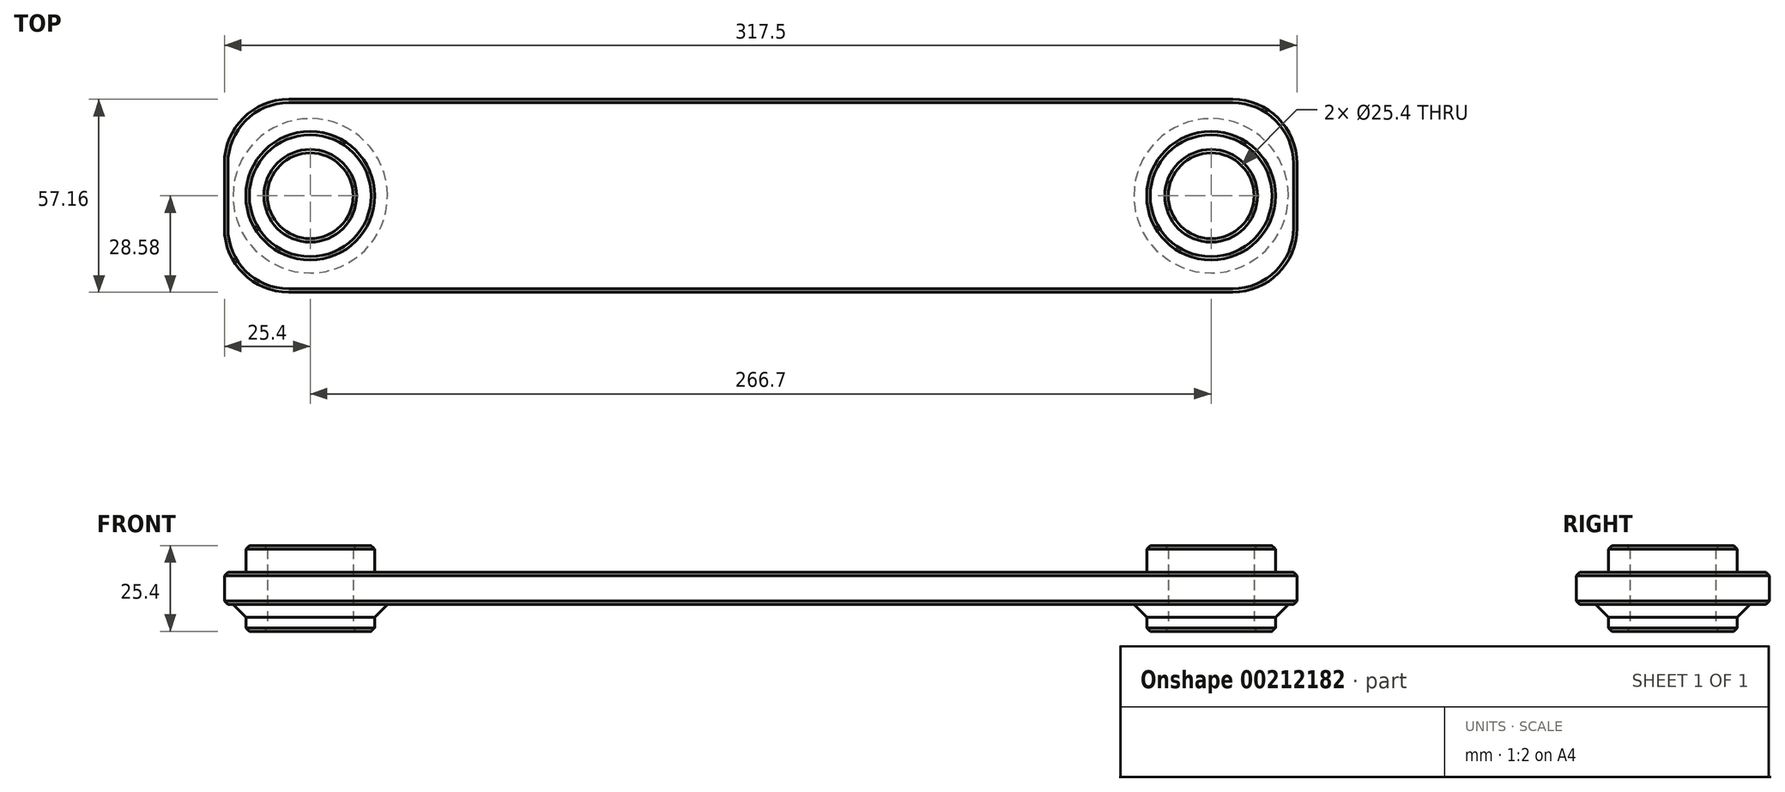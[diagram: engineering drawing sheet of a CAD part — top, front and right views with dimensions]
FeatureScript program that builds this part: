
annotation { "Feature Type Name" : "Feature", "Feature Type Description" : "" }
export const myFeature = defineFeature(function(context is Context, id is Id, definition is map)
    precondition{}
    {
        {
            var Q0;
            Q0=qCreatedBy(makeId("Top.planeOp"),FACE);
            var sketch = newSketch(context, id + "F0", { "sketchPlane" : qUnion([Q0])});
            skLineSegment(sketch, "E0.bottom", {"start": v(139.7, -28.57) * mm, "end": v(-139.7, -28.58) * mm});
            skLineSegment(sketch, "E0.top", {"start": v(139.7, 28.58) * mm, "end": v(-139.7, 28.57) * mm});
            skLineSegment(sketch, "E0.left", {"start": v(158.75, -9.52) * mm, "end": v(158.75, 9.53) * mm});
            skLineSegment(sketch, "E0.right", {"start": v(-158.75, -9.53) * mm, "end": v(-158.75, 9.52) * mm});
            skPoint(sketch, "E0.middle", {"position": v(0, 0) * mm});
            skCircle(sketch, "E1", {"center": v(133.35, 0) * mm, "radius": 12.7 * mm});
            skCircle(sketch, "E2", {"center": v(-133.35, 0) * mm, "radius": 12.7 * mm});
            skLineSegment(sketch, "E3", {"start": v(-133.35, 0) * mm, "end": v(0, 0) * mm, "construction": true});
            skLineSegment(sketch, "E4", {"start": v(0, 0) * mm, "end": v(133.35, 0) * mm, "construction": true});
            skCircle(sketch, "E5", {"center": v(133.35, 0) * mm, "radius": 19.05 * mm});
            skCircle(sketch, "E6", {"center": v(-133.35, 0) * mm, "radius": 19.05 * mm});
            skPoint(sketch, "E7.visualSharp", {"position": v(158.75, -28.57) * mm});
            skArc(sketch, "E7.filletArc", {"start": v(139.7, -28.57) * mm, "mid": v(153.17, -23) * mm, "end": v(158.75, -9.52) * mm});
            skPoint(sketch, "E8.visualSharp", {"position": v(158.75, 28.58) * mm});
            skArc(sketch, "E8.filletArc", {"start": v(158.75, 9.53) * mm, "mid": v(153.17, 23) * mm, "end": v(139.7, 28.58) * mm});
            skPoint(sketch, "E9.visualSharp", {"position": v(-158.75, -28.58) * mm});
            skArc(sketch, "E9.filletArc", {"start": v(-158.75, -9.53) * mm, "mid": v(-153.17, -23) * mm, "end": v(-139.7, -28.58) * mm});
            skPoint(sketch, "E10.visualSharp", {"position": v(-158.75, 28.57) * mm});
            skArc(sketch, "E10.filletArc", {"start": v(-139.7, 28.57) * mm, "mid": v(-153.17, 23) * mm, "end": v(-158.75, 9.52) * mm});
            skSolve(sketch);
        }
        {
            var Q0;
            Q0=makeQuery(id+"F0.imprint","IMPRINT",FACE,{"disambiguationData":[TD([[makeQuery(id+"F0.imprint","IMPRINT",EDGE,{"derivedFrom":sQuery(id+"F0.wireOp",EDGE,"E0.bottom")}),-1.0]])]});
            extrude(context, id + "F1", {"entities" : qUnion([Q0]), "depth" : 4.76 * mm, "hasSecondDirection" : true, "secondDirectionOppositeDirection" : true, "secondDirectionDepth" : 4.76 * mm});
        }
        {
            var Q0;
            Q0=makeQuery(id+"F0.imprint","IMPRINT",FACE,{"disambiguationData":[TD([[makeQuery(id+"F0.imprint","IMPRINT",EDGE,{"derivedFrom":sQuery(id+"F0.wireOp",EDGE,"E2")}),-1.0]])]});
            var Q1;
            Q1=makeQuery(id+"F0.imprint","IMPRINT",FACE,{"disambiguationData":[TD([[makeQuery(id+"F0.imprint","IMPRINT",EDGE,{"derivedFrom":sQuery(id+"F0.wireOp",EDGE,"E1")}),-1.0]])]});
            extrude(context, id + "F2", {"entities" : qUnion([Q0, Q1]), "operationType" : NewBodyOperationType.ADD, "depth" : 12.7 * mm, "hasSecondDirection" : true, "secondDirectionOppositeDirection" : true, "secondDirectionDepth" : 12.7 * mm});
        }
        {
            var Q0;
            Q0=makeQuery(id+"F1.opExtrude","SWEPT_FACE",FACE,{"disambiguationData":[OSD([sQuery(id+"F0.wireOp",EDGE,"E0.bottom")])]});
            var Q1;
            Q1=makeQuery(id+"F1.opExtrude","SWEPT_FACE",FACE,{"disambiguationData":[OSD([sQuery(id+"F0.wireOp",EDGE,"E0.left")])]});
            var Q2;
            Q2=makeQuery(id+"F1.opExtrude","SWEPT_FACE",FACE,{"disambiguationData":[OSD([sQuery(id+"F0.wireOp",EDGE,"E0.top")])]});
            var Q3;
            Q3=makeQuery(id+"F1.opExtrude","SWEPT_FACE",FACE,{"disambiguationData":[OSD([sQuery(id+"F0.wireOp",EDGE,"E0.right")])]});
            var Q4;
            Q4=makeQuery(id+"F2.opExtrude","SWEPT_FACE",FACE,{"disambiguationData":[OSD([sQuery(id+"F0.wireOp",EDGE,"E1")])]});
            var Q5;
            Q5=makeQuery(id+"F2.opExtrude","SWEPT_FACE",FACE,{"disambiguationData":[OSD([sQuery(id+"F0.wireOp",EDGE,"E2")])]});
            var Q6;
            Q6=makeQuery(id+"F2.opExtrude","CAP_EDGE",EDGE,{"disambiguationData":[OSD([sQuery(id+"F0.wireOp",EDGE,"E6")])],"isStart":true});
            var Q7;
            Q7=makeQuery(id+"F2.opExtrude","CAP_EDGE",EDGE,{"disambiguationData":[OSD([sQuery(id+"F0.wireOp",EDGE,"E5")])],"isStart":true});
            var Q8;
            Q8=makeQuery(id+"F2.opExtrude","CAP_EDGE",EDGE,{"disambiguationData":[OSD([sQuery(id+"F0.wireOp",EDGE,"E5")])],"isStart":false});
            var Q9;
            Q9=makeQuery(id+"F2.opExtrude","CAP_EDGE",EDGE,{"disambiguationData":[OSD([sQuery(id+"F0.wireOp",EDGE,"E6")])],"isStart":false});
            chamfer(context, id + "F3", {"entities" : qUnion([Q0, Q1, Q2, Q3, Q4, Q5, Q6, Q7, Q8, Q9]), "width" : 1.02 * mm, "tangentPropagation" : true});
        }
        {
            var Q0;
            Q0=makeQuery(id+"F1.opExtrude","CAP_EDGE",EDGE,{"disambiguationData":[OSD([sQuery(id+"F0.wireOp",EDGE,"E6")])],"isStart":false});
            var Q1;
            Q1=makeQuery(id+"F1.opExtrude","CAP_EDGE",EDGE,{"disambiguationData":[OSD([sQuery(id+"F0.wireOp",EDGE,"E6")])],"isStart":true});
            var Q2;
            Q2=makeQuery(id+"F1.opExtrude","CAP_EDGE",EDGE,{"disambiguationData":[OSD([sQuery(id+"F0.wireOp",EDGE,"E5")])],"isStart":true});
            var Q3;
            Q3=makeQuery(id+"F1.opExtrude","CAP_EDGE",EDGE,{"disambiguationData":[OSD([sQuery(id+"F0.wireOp",EDGE,"E5")])],"isStart":false});
            chamfer(context, id + "F4", {"entities" : qUnion([Q0, Q1, Q2, Q3]), "width" : 3.8 * mm, "tangentPropagation" : true});
        }
    });
